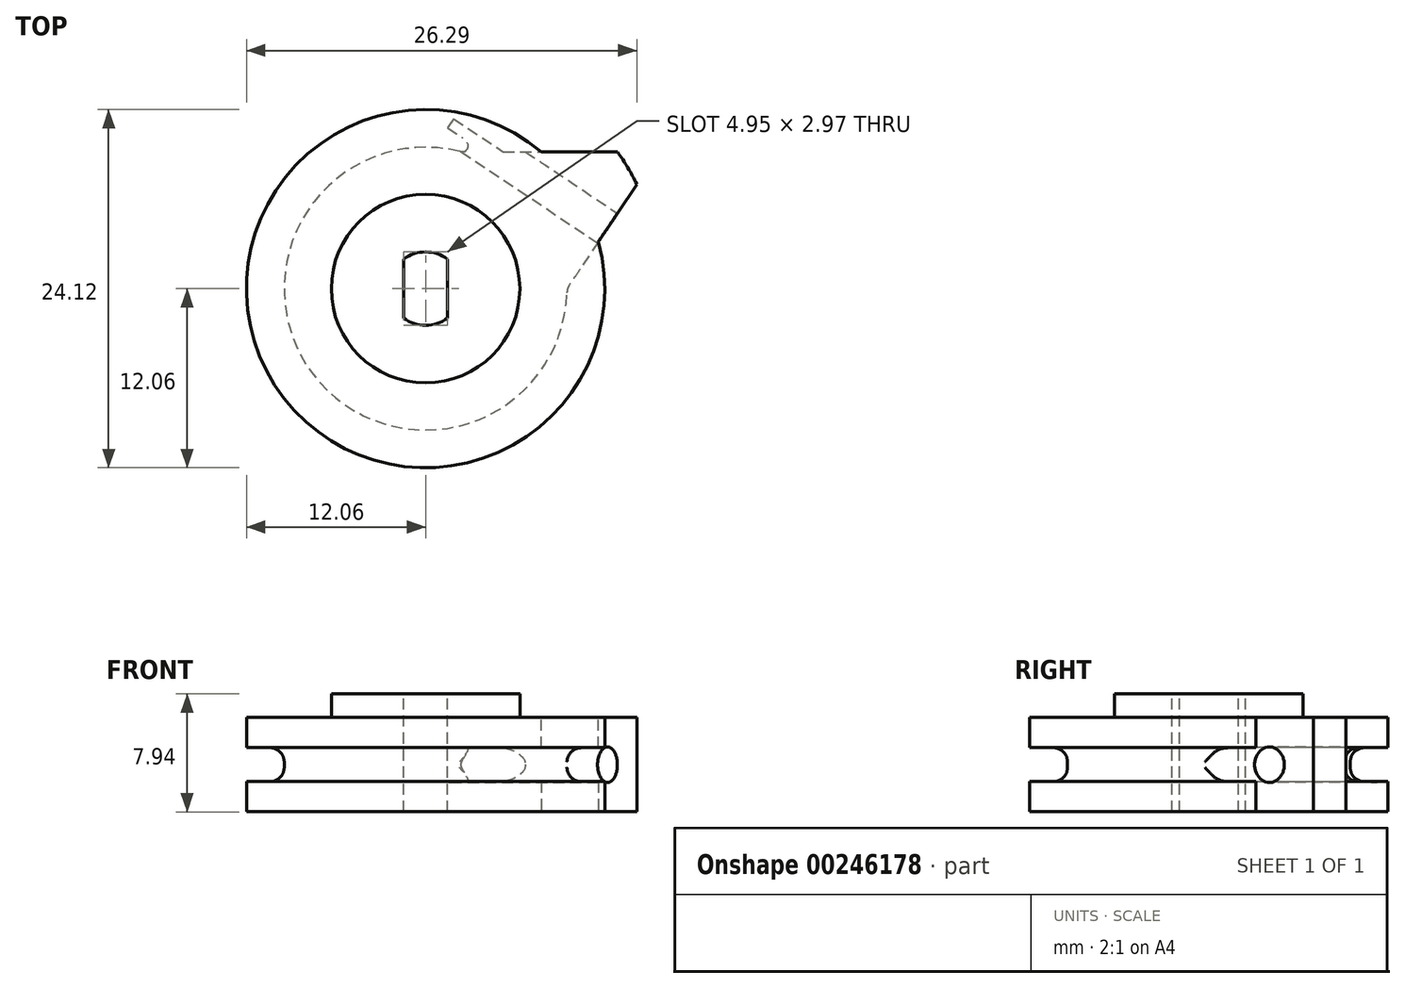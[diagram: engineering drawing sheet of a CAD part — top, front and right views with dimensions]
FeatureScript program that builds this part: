
annotation { "Feature Type Name" : "Feature", "Feature Type Description" : "" }
export const myFeature = defineFeature(function(context is Context, id is Id, definition is map)
    precondition{}
    {
        {
            var Q0;
            Q0=qCreatedBy(makeId("Top.planeOp"),FACE);
            var sketch = newSketch(context, id + "F0", { "sketchPlane" : qUnion([Q0])});
            skArc(sketch, "E0", {"start": v(-1.49, -1.98) * mm, "mid": v(0, -2.48) * mm, "end": v(1.49, -1.98) * mm});
            skLineSegment(sketch, "E1", {"start": v(-1.49, -1.98) * mm, "end": v(-1.49, 1.98) * mm});
            skLineSegment(sketch, "E2", {"start": v(1.49, -1.98) * mm, "end": v(1.49, 1.98) * mm});
            skArc(sketch, "E3.trimOffspring", {"start": v(1.49, 1.98) * mm, "mid": v(0, 2.48) * mm, "end": v(-1.49, 1.98) * mm});
            skPoint(sketch, "E4.orphan", {"position": v(1.49, 5.26) * mm});
            skPoint(sketch, "E5.orphan", {"position": v(-1.49, 5.26) * mm});
            skPoint(sketch, "E6.orphan", {"position": v(-1.49, -3.31) * mm});
            skCircle(sketch, "E7", {"center": v(0, 0) * mm, "radius": 6.35 * mm});
            skSolve(sketch);
        }
        {
            var Q0;
            Q0=makeQuery(id+"F0.imprint","IMPRINT",FACE,{"disambiguationData":[TD([[makeQuery(id+"F0.imprint","IMPRINT",EDGE,{"derivedFrom":sQuery(id+"F0.wireOp",EDGE,"E0")}),-1.0]])]});
            extrude(context, id + "F1", {"entities" : qUnion([Q0]), "oppositeDirection" : true, "depth" : 1.59 * mm});
        }
        {
            var Q0;
            Q0=makeQuery(id+"F1.opExtrude","CAP_FACE",FACE,{"disambiguationData":[OSD([sQuery(id+"F0.wireOp",EDGE,"E0"),sQuery(id+"F0.wireOp",EDGE,"E1"),sQuery(id+"F0.wireOp",EDGE,"E2"),sQuery(id+"F0.wireOp",EDGE,"E3.trimOffspring"),sQuery(id+"F0.wireOp",EDGE,"E7")])],"isStart":false});
            var sketch = newSketch(context, id + "F2", { "sketchPlane" : qUnion([Q0])});
            skCircle(sketch, "E8", {"center": v(0, 0) * mm, "radius": 9.53 * mm});
            skSolve(sketch);
        }
        {
            var Q0;
            Q0=makeQuery(id+"F2.imprint","IMPRINT",FACE,{"disambiguationData":[TD([[makeQuery(id+"F2.imprint","IMPRINT",EDGE,{"derivedFrom":sQuery(id+"F2.wireOp",EDGE,"E8")}),1.0]])]});
            var Q1;
            Q1=makeQuery(id+"F2.imprint","IMPRINT",FACE,{"disambiguationData":[TD([[makeQuery(id+"F2.imprint","IMPRINT",EDGE,{"derivedFrom":makeQuery(id+"F1.opExtrude","CAP_EDGE",EDGE,{"disambiguationData":[OSD([sQuery(id+"F0.wireOp",EDGE,"E0")])],"isStart":false})}),1.0]])]});
            extrude(context, id + "F3", {"entities" : qUnion([Q0, Q1]), "operationType" : NewBodyOperationType.ADD, "depth" : 6.35 * mm});
        }
        {
            var Q0;
            Q0=makeQuery(id+"F3.opExtrude","CAP_FACE",FACE,{"disambiguationData":[OSD([sQuery(id+"F0.wireOp",EDGE,"E0"),sQuery(id+"F0.wireOp",EDGE,"E1"),sQuery(id+"F0.wireOp",EDGE,"E2"),sQuery(id+"F0.wireOp",EDGE,"E3.trimOffspring"),sQuery(id+"F2.wireOp",EDGE,"E8")])],"isStart":false});
            var sketch = newSketch(context, id + "F4", { "sketchPlane" : qUnion([Q0])});
            skCircle(sketch, "E9", {"center": v(0, 0) * mm, "radius": 12.07 * mm});
            skSolve(sketch);
        }
        {
            var Q0;
            Q0=makeQuery(id+"F4.imprint","IMPRINT",FACE,{"disambiguationData":[TD([[makeQuery(id+"F4.imprint","IMPRINT",EDGE,{"derivedFrom":sQuery(id+"F4.wireOp",EDGE,"E9")}),1.0]])]});
            extrude(context, id + "F5", {"entities" : qUnion([Q0]), "operationType" : NewBodyOperationType.ADD, "oppositeDirection" : true, "depth" : 2.03 * mm});
        }
        {
            var Q0;
            Q0=makeQuery(id+"F3.opExtrude","CAP_FACE",FACE,{"disambiguationData":[OSD([sQuery(id+"F0.wireOp",EDGE,"E0"),sQuery(id+"F0.wireOp",EDGE,"E1"),sQuery(id+"F0.wireOp",EDGE,"E2"),sQuery(id+"F0.wireOp",EDGE,"E3.trimOffspring"),sQuery(id+"F2.wireOp",EDGE,"E8")])],"isStart":true});
            var sketch = newSketch(context, id + "F6", { "sketchPlane" : qUnion([Q0])});
            skCircle(sketch, "E10", {"center": v(0, 0) * mm, "radius": 12.06 * mm});
            skSolve(sketch);
        }
        {
            var Q0;
            Q0=makeQuery(id+"F6.imprint","IMPRINT",FACE,{"disambiguationData":[TD([[makeQuery(id+"F6.imprint","IMPRINT",EDGE,{"derivedFrom":sQuery(id+"F6.wireOp",EDGE,"E10")}),1.0]])]});
            extrude(context, id + "F7", {"entities" : qUnion([Q0]), "operationType" : NewBodyOperationType.ADD, "oppositeDirection" : true, "depth" : 2.03 * mm});
        }
        {
            var Q0;
            {var subQ0=sQuery(id+"F2.wireOp",EDGE,"E8");Q0=makeQuery(id+"F7.boolean.opBoolean","MERGE",FACE,{"derivedFrom":[makeQuery(id+"F3.opExtrude","CAP_FACE",FACE,{"disambiguationData":[OSD([sQuery(id+"F0.wireOp",EDGE,"E0"),sQuery(id+"F0.wireOp",EDGE,"E1"),sQuery(id+"F0.wireOp",EDGE,"E2"),sQuery(id+"F0.wireOp",EDGE,"E3.trimOffspring"),subQ0])],"isStart":true}),makeQuery(id+"F7.opExtrude","CAP_FACE",FACE,{"disambiguationData":[OSD([subQ0,sQuery(id+"F6.wireOp",EDGE,"E10")])],"isStart":true})]});}
            var sketch = newSketch(context, id + "F8", { "sketchPlane" : qUnion([Q0])});
            skLineSegment(sketch, "E11", {"start": v(9.53, 0) * mm, "end": v(14.23, 7.04) * mm});
            skLineSegment(sketch, "E12", {"start": v(12.92, 9.22) * mm, "end": v(2.4, 9.22) * mm});
            skArc(sketch, "E13", {"start": v(9.53, 0) * mm, "mid": v(7.53, 5.83) * mm, "end": v(2.4, 9.22) * mm});
            skArc(sketch, "E14", {"start": v(14.23, 7.04) * mm, "mid": v(13.62, 8.16) * mm, "end": v(12.92, 9.22) * mm});
            skLineSegment(sketch, "E15", {"start": v(11.88, 3.52) * mm, "end": v(5.3, 7.92) * mm, "construction": true});
            skSolve(sketch);
        }
        {
            var Q0;
            {var subQ0=sQuery(id+"F8.wireOp",EDGE,"E14");Q0=makeQuery(id+"F8.imprint","IMPRINT",FACE,{"disambiguationData":[TD([[makeQuery(id+"F8.imprint","IMPRINT",EDGE,{"derivedFrom":subQ0}),1.0]])]});}
            var Q1;
            {var subQ0=sQuery(id+"F8.wireOp",EDGE,"E13");Q1=makeQuery(id+"F8.imprint","IMPRINT",FACE,{"disambiguationData":[TD([[makeQuery(id+"F8.imprint","IMPRINT",EDGE,{"derivedFrom":subQ0}),-1.0]])]});}
            extrude(context, id + "F9", {"entities" : qUnion([Q0, Q1]), "operationType" : NewBodyOperationType.ADD, "oppositeDirection" : true, "depth" : 6.35 * mm});
        }
        {
            var Q0;
            Q0=makeQuery(id+"F9.opExtrude","SWEPT_FACE",FACE,{"disambiguationData":[OSD([sQuery(id+"F8.wireOp",EDGE,"E11")])]});
            var sketch = newSketch(context, id + "F10", { "sketchPlane" : qUnion([Q0])});
            skCircle(sketch, "E16", {"center": v(10.2, -4.76) * mm, "radius": 1.2 * mm});
            skSolve(sketch);
        }
        {
            var Q0;
            Q0=makeQuery(id+"F10.imprint","IMPRINT",FACE,{"disambiguationData":[TD([[makeQuery(id+"F10.imprint","IMPRINT",EDGE,{"derivedFrom":sQuery(id+"F10.wireOp",EDGE,"E16")}),1.0]])]});
            extrude(context, id + "F11", {"entities" : qUnion([Q0]), "operationType" : NewBodyOperationType.REMOVE, "oppositeDirection" : true, "depth" : 12.7 * mm});
        }
        {
            var Q0;
            Q0=makeQuery(id+"F3.opExtrude","SWEPT_FACE",FACE,{"disambiguationData":[OSD([sQuery(id+"F2.wireOp",EDGE,"E8")])]});
            fillet(context, id + "F12", {"entities" : qUnion([Q0]), "radius" : 0.95 * mm, "tangentPropagation" : true, "allowEdgeOverflow" : false});
        }
    });
